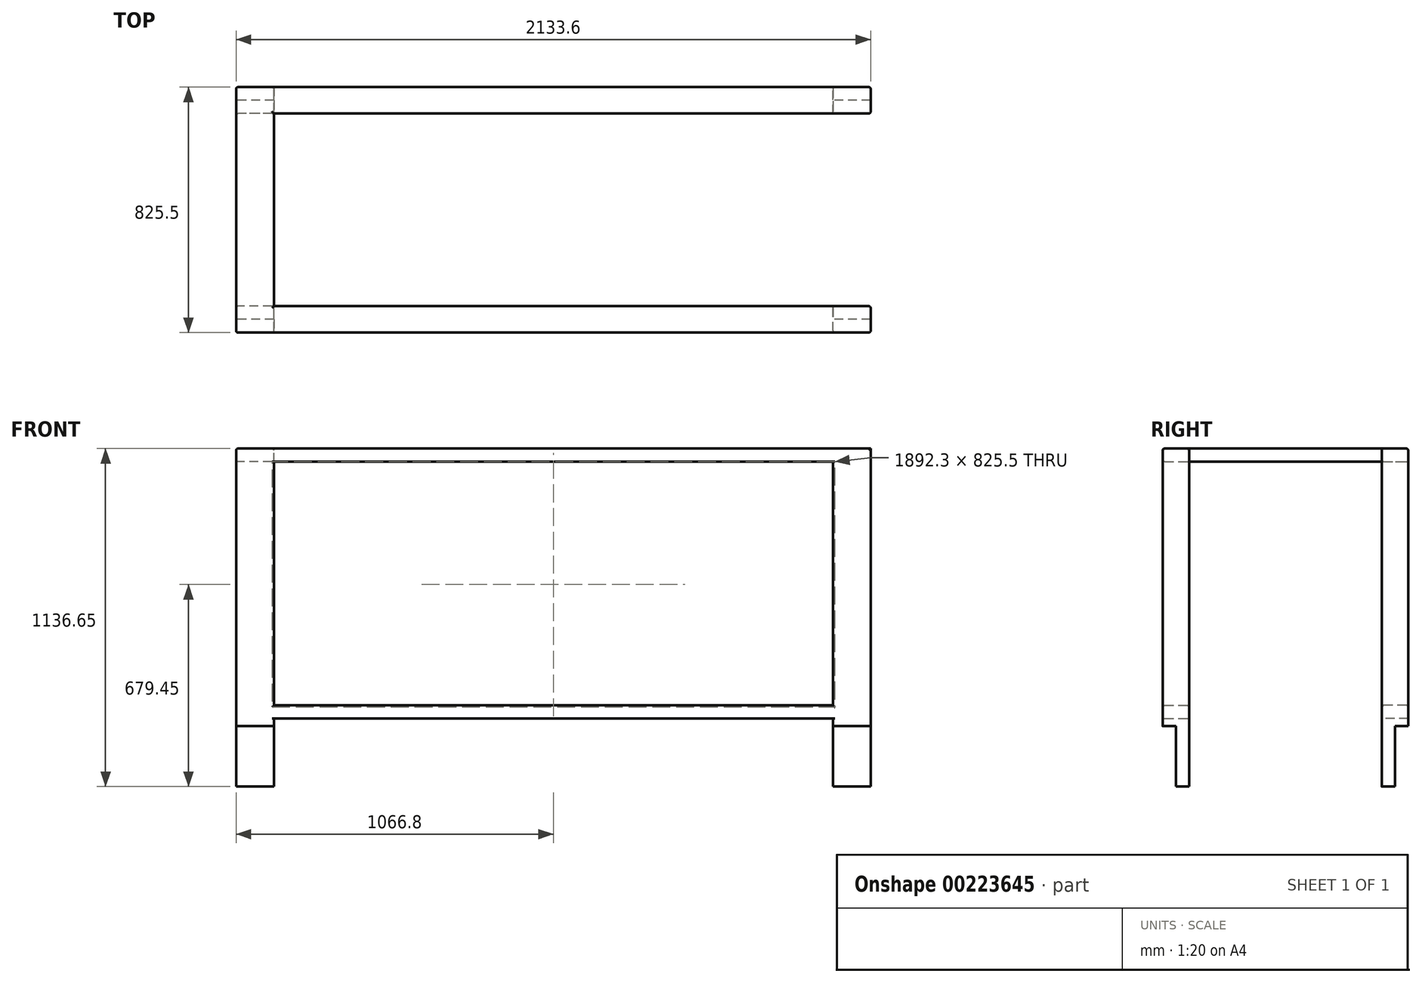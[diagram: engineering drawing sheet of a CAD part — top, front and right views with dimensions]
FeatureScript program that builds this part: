
annotation { "Feature Type Name" : "Feature", "Feature Type Description" : "" }
export const myFeature = defineFeature(function(context is Context, id is Id, definition is map)
    precondition{}
    {
        {
            var Q0;
            Q0=qCreatedBy(makeId("Top.planeOp"),FACE);
            var sketch = newSketch(context, id + "F0", { "sketchPlane" : qUnion([Q0])});
            skLineSegment(sketch, "E0.bottom", {"start": v(75.95, 0) * mm, "end": v(-51.05, 0) * mm});
            skLineSegment(sketch, "E0.top", {"start": v(75.95, -44.45) * mm, "end": v(-51.05, -44.45) * mm});
            skLineSegment(sketch, "E0.left", {"start": v(75.95, 0) * mm, "end": v(75.95, -44.45) * mm});
            skLineSegment(sketch, "E0.right", {"start": v(-51.05, 0) * mm, "end": v(-51.05, -44.45) * mm});
            skSolve(sketch);
        }
        {
            var Q0;
            Q0=makeQuery(id+"F0.imprint","IMPRINT",FACE,{"disambiguationData":[TD([[makeQuery(id+"F0.imprint","IMPRINT",EDGE,{"derivedFrom":sQuery(id+"F0.wireOp",EDGE,"E0.bottom")}),1.0]])]});
            extrude(context, id + "F1", {"entities" : qUnion([Q0]), "depth" : 889 * mm});
        }
        {
            var Q0;
            Q0=makeQuery(id+"F1.opExtrude","CAP_FACE",FACE,{"disambiguationData":[OSD([sQuery(id+"F0.wireOp",EDGE,"E0.bottom"),sQuery(id+"F0.wireOp",EDGE,"E0.top"),sQuery(id+"F0.wireOp",EDGE,"E0.left"),sQuery(id+"F0.wireOp",EDGE,"E0.right")])],"isStart":false});
            var sketch = newSketch(context, id + "F2", { "sketchPlane" : qUnion([Q0])});
            skLineSegment(sketch, "E1.bottom", {"start": v(75.95, 0) * mm, "end": v(-51.05, 0) * mm});
            skLineSegment(sketch, "E1.top", {"start": v(75.95, 44.45) * mm, "end": v(-51.05, 44.45) * mm});
            skLineSegment(sketch, "E1.left", {"start": v(75.95, 0) * mm, "end": v(75.95, 44.45) * mm});
            skLineSegment(sketch, "E1.right", {"start": v(-51.05, 0) * mm, "end": v(-51.05, 44.45) * mm});
            skSolve(sketch);
        }
        {
            var Q0;
            Q0=makeQuery(id+"F2.imprint","IMPRINT",FACE,{"disambiguationData":[TD([[makeQuery(id+"F2.imprint","IMPRINT",EDGE,{"derivedFrom":sQuery(id+"F2.wireOp",EDGE,"E1.bottom")}),-1.0]])]});
            extrude(context, id + "F3", {"entities" : qUnion([Q0]), "oppositeDirection" : true, "depth" : 1092.2 * mm});
        }
        {
            var Q0;
            Q0=makeQuery(id+"F3.boolean.opBoolean","MERGE",FACE,{"derivedFrom":[makeQuery(id+"F1.opExtrude","SWEPT_FACE",FACE,{"disambiguationData":[OSD([sQuery(id+"F0.wireOp",EDGE,"E0.left")])]}),makeQuery(id+"F3.opExtrude","SWEPT_FACE",FACE,{"disambiguationData":[OSD([sQuery(id+"F2.wireOp",EDGE,"E1.left")])]})]});
            var sketch = newSketch(context, id + "F4", { "sketchPlane" : qUnion([Q0])});
            skLineSegment(sketch, "E2.bottom", {"start": v(-44.45, 25.4) * mm, "end": v(44.45, 25.4) * mm});
            skLineSegment(sketch, "E2.top", {"start": v(-44.45, 69.85) * mm, "end": v(44.45, 69.85) * mm});
            skLineSegment(sketch, "E2.left", {"start": v(-44.45, 25.4) * mm, "end": v(-44.45, 69.85) * mm});
            skLineSegment(sketch, "E2.right", {"start": v(44.45, 25.4) * mm, "end": v(44.45, 69.85) * mm});
            skSolve(sketch);
        }
        {
            var Q0;
            Q0=makeQuery(id+"F4.imprint","IMPRINT",FACE,{"disambiguationData":[TD([[makeQuery(id+"F4.imprint","IMPRINT",EDGE,{"derivedFrom":sQuery(id+"F4.wireOp",EDGE,"E2.bottom")}),1.0]])]});
            extrude(context, id + "F5", {"entities" : qUnion([Q0]), "depth" : 1879.6 * mm});
        }
        {
            var Q0;
            Q0=makeQuery(id+"F3.opExtrude","SWEPT_FACE",FACE,{"disambiguationData":[OSD([sQuery(id+"F2.wireOp",EDGE,"E1.right")])]});
            var sketch = newSketch(context, id + "F6", { "sketchPlane" : qUnion([Q0])});
            skLineSegment(sketch, "E3.bottom", {"start": v(-44.45, 889) * mm, "end": v(44.45, 889) * mm});
            skLineSegment(sketch, "E3.top", {"start": v(-44.45, 933.45) * mm, "end": v(44.45, 933.45) * mm});
            skLineSegment(sketch, "E3.left", {"start": v(-44.45, 889) * mm, "end": v(-44.45, 933.45) * mm});
            skLineSegment(sketch, "E3.right", {"start": v(44.45, 889) * mm, "end": v(44.45, 933.45) * mm});
            skSolve(sketch);
        }
        {
            var Q0;
            Q0=makeQuery(id+"F6.imprint","IMPRINT",FACE,{"disambiguationData":[TD([[makeQuery(id+"F6.imprint","IMPRINT",EDGE,{"derivedFrom":sQuery(id+"F6.wireOp",EDGE,"E3.top")}),-1.0]])]});
            extrude(context, id + "F7", {"entities" : qUnion([Q0]), "oppositeDirection" : true, "depth" : 2133.6 * mm});
        }
        {
            var Q0;
            Q0=makeQuery(id+"F7.opExtrude","SWEPT_FACE",FACE,{"disambiguationData":[OSD([sQuery(id+"F6.wireOp",EDGE,"E3.bottom")])]});
            var sketch = newSketch(context, id + "F8", { "sketchPlane" : qUnion([Q0])});
            skLineSegment(sketch, "E4.bottom", {"start": v(2082.55, -44.45) * mm, "end": v(1955.55, -44.45) * mm});
            skLineSegment(sketch, "E4.top", {"start": v(2082.55, 0) * mm, "end": v(1955.55, 0) * mm});
            skLineSegment(sketch, "E4.left", {"start": v(2082.55, -44.45) * mm, "end": v(2082.55, 0) * mm});
            skLineSegment(sketch, "E4.right", {"start": v(1955.55, -44.45) * mm, "end": v(1955.55, 0) * mm});
            skSolve(sketch);
        }
        {
            var Q0;
            Q0=makeQuery(id+"F8.imprint","IMPRINT",FACE,{"disambiguationData":[TD([[makeQuery(id+"F8.imprint","IMPRINT",EDGE,{"derivedFrom":sQuery(id+"F8.wireOp",EDGE,"E4.bottom")}),-1.0]])]});
            extrude(context, id + "F9", {"entities" : qUnion([Q0]), "depth" : 1092.2 * mm});
        }
        {
            var Q0;
            Q0=makeQuery(id+"F7.opExtrude","SWEPT_FACE",FACE,{"disambiguationData":[OSD([sQuery(id+"F6.wireOp",EDGE,"E3.bottom")])]});
            var sketch = newSketch(context, id + "F10", { "sketchPlane" : qUnion([Q0])});
            skLineSegment(sketch, "E5.bottom", {"start": v(2082.55, 44.45) * mm, "end": v(1955.55, 44.45) * mm});
            skLineSegment(sketch, "E5.top", {"start": v(2082.55, 0) * mm, "end": v(1955.55, 0) * mm});
            skLineSegment(sketch, "E5.left", {"start": v(2082.55, 44.45) * mm, "end": v(2082.55, 0) * mm});
            skLineSegment(sketch, "E5.right", {"start": v(1955.55, 44.45) * mm, "end": v(1955.55, 0) * mm});
            skSolve(sketch);
        }
        {
            var Q0;
            Q0=makeQuery(id+"F10.imprint","IMPRINT",FACE,{"disambiguationData":[TD([[makeQuery(id+"F10.imprint","IMPRINT",EDGE,{"derivedFrom":sQuery(id+"F10.wireOp",EDGE,"E5.bottom")}),1.0]])]});
            extrude(context, id + "F11", {"entities" : qUnion([Q0]), "depth" : 889 * mm});
        }
        {
            var Q0;
            Q0=makeQuery(id+"F7.opExtrude","SWEPT_FACE",FACE,{"disambiguationData":[OSD([sQuery(id+"F6.wireOp",EDGE,"E3.top")])]});
            var sketch = newSketch(context, id + "F12", { "sketchPlane" : qUnion([Q0])});
            skLineSegment(sketch, "E6", {"start": v(-51.05, -44.45) * mm, "end": v(-51.05, 44.45) * mm});
            skLineSegment(sketch, "E7", {"start": v(-51.05, 44.45) * mm, "end": v(75.95, 44.45) * mm});
            skLineSegment(sketch, "E8", {"start": v(75.95, 44.45) * mm, "end": v(-51.05, -44.45) * mm});
            skSolve(sketch);
        }
        {
            var Q0;
            Q0=makeQuery(id+"F12.imprint","IMPRINT",FACE,{"disambiguationData":[TD([[makeQuery(id+"F12.imprint","IMPRINT",EDGE,{"derivedFrom":sQuery(id+"F12.wireOp",EDGE,"E6")}),1.0]])]});
            extrude(context, id + "F13", {"entities" : qUnion([Q0]), "oppositeDirection" : true, "depth" : 44.45 * mm});
        }
        {
            var Q0;
            Q0=makeQuery(id+"F13.opExtrude","SWEPT_BODY",BODY,{"disambiguationData":[OSD([sQuery(id+"F12.wireOp",EDGE,"E6"),sQuery(id+"F12.wireOp",EDGE,"E7"),sQuery(id+"F12.wireOp",EDGE,"E8")])]});
            var Q1;
            Q1=makeQuery(id+"F7.opExtrude","SWEPT_BODY",BODY,{"disambiguationData":[OSD([sQuery(id+"F6.wireOp",EDGE,"E3.bottom"),sQuery(id+"F6.wireOp",EDGE,"E3.top"),sQuery(id+"F6.wireOp",EDGE,"E3.left"),sQuery(id+"F6.wireOp",EDGE,"E3.right")])]});
            booleanBodies(context, id + "F14", {"operationType" : BooleanOperationType.SUBTRACTION, "tools" : qUnion([Q0]), "targets" : qUnion([Q1])});
        }
        {
            var Q0;
            Q0=makeQuery(id+"F3.opExtrude","CAP_FACE",FACE,{"disambiguationData":[OSD([sQuery(id+"F2.wireOp",EDGE,"E1.bottom"),sQuery(id+"F2.wireOp",EDGE,"E1.top"),sQuery(id+"F2.wireOp",EDGE,"E1.left"),sQuery(id+"F2.wireOp",EDGE,"E1.right")])],"isStart":true});
            var sketch = newSketch(context, id + "F15", { "sketchPlane" : qUnion([Q0])});
            skLineSegment(sketch, "E9", {"start": v(75.95, 44.45) * mm, "end": v(-51.05, -44.45) * mm});
            skLineSegment(sketch, "E10", {"start": v(-51.05, -44.45) * mm, "end": v(-51.05, 44.45) * mm});
            skLineSegment(sketch, "E11", {"start": v(-51.05, 44.45) * mm, "end": v(75.95, 44.45) * mm});
            skSolve(sketch);
        }
        {
            var Q0;
            {var subQ0=sQuery(id+"F15.wireOp",EDGE,"E10");var subQ1=makeQuery(id+"F3.opExtrude","CAP_EDGE",EDGE,{"disambiguationData":[OSD([sQuery(id+"F2.wireOp",EDGE,"E1.bottom")])],"isStart":true});var subQ2=makeQuery(id+"F15.imprint","INTERSECT",VERTEX,{"derivedFrom":[subQ1,subQ0]});Q0=makeQuery(id+"F15.imprint","IMPRINT",FACE,{"disambiguationData":[TD([[makeQuery(id+"F15.imprint","IMPRINT",EDGE,{"disambiguationData":[TD([[subQ2,1.0]])],"derivedFrom":subQ0}),-1.0]])]});}
            var Q1;
            {var subQ3=sQuery(id+"F15.wireOp",EDGE,"E11");Q1=makeQuery(id+"F15.imprint","IMPRINT",FACE,{"disambiguationData":[TD([[makeQuery(id+"F15.imprint","IMPRINT",EDGE,{"derivedFrom":subQ3}),1.0]])]});}
            extrude(context, id + "F16", {"entities" : qUnion([Q0, Q1]), "depth" : 44.45 * mm});
        }
        {
            var Q0;
            Q0=makeQuery(id+"F16.opExtrude","SWEPT_FACE",FACE,{"disambiguationData":[OSD([sQuery(id+"F15.wireOp",EDGE,"E11")])]});
            extrude(context, id + "F17", {"entities" : qUnion([Q0]), "operationType" : NewBodyOperationType.ADD, "depth" : 323.85 * mm});
        }
        {
            var Q0;
            {var subQ0=sQuery(id+"F15.wireOp",EDGE,"E11");Q0=makeQuery(id+"F17.boolean.opBoolean","MERGE",FACE,{"derivedFrom":[makeQuery(id+"F16.opExtrude","CAP_FACE",FACE,{"disambiguationData":[OSD([sQuery(id+"F15.wireOp",EDGE,"E10"),sQuery(id+"F15.wireOp",EDGE,"E9"),subQ0])],"isStart":false}),makeQuery(id+"F17.opExtrude","SWEPT_FACE",FACE,{"disambiguationData":[OSD([subQ0]),TDD([makeQuery(id+"F16.opExtrude","CAP_EDGE",EDGE,{"disambiguationData":[OSD([subQ0])],"isStart":false})])]})]});}
            var sketch = newSketch(context, id + "F18", { "sketchPlane" : qUnion([Q0])});
            skLineSegment(sketch, "E12", {"start": v(75.95, 368.3) * mm, "end": v(-51.05, 368.3) * mm});
            skLineSegment(sketch, "E13", {"start": v(-51.05, 368.3) * mm, "end": v(-51.05, 457.2) * mm});
            skLineSegment(sketch, "E14", {"start": v(-51.05, 457.2) * mm, "end": v(75.95, 368.3) * mm});
            skSolve(sketch);
        }
        {
            var Q0;
            Q0=makeQuery(id+"F18.imprint","IMPRINT",FACE,{"disambiguationData":[TD([[makeQuery(id+"F18.imprint","IMPRINT",EDGE,{"derivedFrom":sQuery(id+"F18.wireOp",EDGE,"E12")}),-1.0]])]});
            extrude(context, id + "F19", {"entities" : qUnion([Q0]), "operationType" : NewBodyOperationType.ADD, "oppositeDirection" : true, "depth" : 44.45 * mm});
        }
        {
            var Q0;
            Q0=qCreatedBy(makeId("Front.planeOp"),FACE);
            cPlane(context, id + "F20", {"entities" : qUnion([Q0]), "cplaneType" : CPlaneType.OFFSET, "offset" : 368.3 * mm, "oppositeDirection" : true, "width" : 152.4 * mm, "height" : 152.4 * mm});
        }
        {
            var Q0;
            Q0=makeQuery(id+"F7.opExtrude","SWEPT_BODY",BODY,{"disambiguationData":[OSD([sQuery(id+"F6.wireOp",EDGE,"E3.bottom"),sQuery(id+"F6.wireOp",EDGE,"E3.top"),sQuery(id+"F6.wireOp",EDGE,"E3.left"),sQuery(id+"F6.wireOp",EDGE,"E3.right")])]});
            var Q1;
            Q1=makeQuery(id+"F11.opExtrude","SWEPT_BODY",BODY,{"disambiguationData":[OSD([sQuery(id+"F10.wireOp",EDGE,"E5.bottom"),sQuery(id+"F10.wireOp",EDGE,"E5.top"),sQuery(id+"F10.wireOp",EDGE,"E5.left"),sQuery(id+"F10.wireOp",EDGE,"E5.right")])]});
            var Q2;
            Q2=makeQuery(id+"F9.opExtrude","SWEPT_BODY",BODY,{"disambiguationData":[OSD([sQuery(id+"F8.wireOp",EDGE,"E4.bottom"),sQuery(id+"F8.wireOp",EDGE,"E4.top"),sQuery(id+"F8.wireOp",EDGE,"E4.left"),sQuery(id+"F8.wireOp",EDGE,"E4.right")])]});
            var Q3;
            Q3=makeQuery(id+"F5.opExtrude","SWEPT_BODY",BODY,{"disambiguationData":[OSD([sQuery(id+"F4.wireOp",EDGE,"E2.bottom"),sQuery(id+"F4.wireOp",EDGE,"E2.top"),sQuery(id+"F4.wireOp",EDGE,"E2.left"),sQuery(id+"F4.wireOp",EDGE,"E2.right")])]});
            var Q4;
            Q4=makeQuery(id+"F16.opExtrude","SWEPT_BODY",BODY,{"disambiguationData":[OSD([sQuery(id+"F15.wireOp",EDGE,"E10"),sQuery(id+"F15.wireOp",EDGE,"E9"),sQuery(id+"F15.wireOp",EDGE,"E11")])]});
            var Q5;
            Q5=makeQuery(id+"F3.opExtrude","SWEPT_BODY",BODY,{"disambiguationData":[OSD([sQuery(id+"F2.wireOp",EDGE,"E1.bottom"),sQuery(id+"F2.wireOp",EDGE,"E1.top"),sQuery(id+"F2.wireOp",EDGE,"E1.left"),sQuery(id+"F2.wireOp",EDGE,"E1.right")])]});
            var Q6;
            Q6=makeQuery(id+"F1.opExtrude","SWEPT_BODY",BODY,{"disambiguationData":[OSD([sQuery(id+"F0.wireOp",EDGE,"E0.bottom"),sQuery(id+"F0.wireOp",EDGE,"E0.top"),sQuery(id+"F0.wireOp",EDGE,"E0.left"),sQuery(id+"F0.wireOp",EDGE,"E0.right")])]});
            var Q7;
            Q7=qCreatedBy(id+"F20.planeOp",FACE);
            mirror(context, id + "F21", {"operationType" : NewBodyOperationType.ADD, "entities" : qUnion([Q0, Q1, Q2, Q3, Q4, Q5, Q6]), "mirrorPlane" : qUnion([Q7])});
        }
        {
            var Q0;
            Q0=makeQuery(id+"F21.opPattern","COPY",EDGE,{"derivedFrom":makeQuery(id+"F5.opExtrude","SWEPT_EDGE",EDGE,{"disambiguationData":[OSD([sQuery(id+"F0.wireOp",EDGE,"E0.top"),sQuery(id+"F0.wireOp",EDGE,"E0.left"),sQuery(id+"F4.wireOp",EDGE,"E2.top"),sQuery(id+"F4.wireOp",EDGE,"E2.left")])]}),"instanceName":"1"});
            var Q1;
            Q1=makeQuery(id+"F21.opPattern","COPY",EDGE,{"derivedFrom":makeQuery(id+"F5.opExtrude","SWEPT_EDGE",EDGE,{"disambiguationData":[OSD([sQuery(id+"F2.wireOp",EDGE,"E1.top"),sQuery(id+"F2.wireOp",EDGE,"E1.left"),sQuery(id+"F4.wireOp",EDGE,"E2.top"),sQuery(id+"F4.wireOp",EDGE,"E2.right")])]}),"instanceName":"1"});
            var Q2;
            Q2=makeQuery(id+"F21.opPattern","COPY",EDGE,{"derivedFrom":makeQuery(id+"F7.opExtrude","SWEPT_EDGE",EDGE,{"disambiguationData":[OSD([sQuery(id+"F6.wireOp",EDGE,"E3.top"),sQuery(id+"F6.wireOp",EDGE,"E3.right")])]}),"instanceName":"1"});
            var Q3;
            Q3=makeQuery(id+"F21.opPattern","COPY",EDGE,{"derivedFrom":makeQuery(id+"F7.opExtrude","SWEPT_EDGE",EDGE,{"disambiguationData":[OSD([sQuery(id+"F6.wireOp",EDGE,"E3.top"),sQuery(id+"F6.wireOp",EDGE,"E3.left")])]}),"instanceName":"1"});
            var Q4;
            Q4=makeQuery(id+"F21.opPattern","COPY",EDGE,{"derivedFrom":makeQuery(id+"F7.opExtrude","CAP_EDGE",EDGE,{"disambiguationData":[OSD([sQuery(id+"F6.wireOp",EDGE,"E3.top")])],"isStart":false}),"instanceName":"1"});
            var Q5;
            Q5=makeQuery(id+"F21.boolean.opBoolean","MERGE",EDGE,{"derivedFrom":[makeQuery(id+"F21.opPattern","COPY",EDGE,{"derivedFrom":makeQuery(id+"F7.opExtrude","CAP_EDGE",EDGE,{"disambiguationData":[OSD([sQuery(id+"F6.wireOp",EDGE,"E3.right")])],"isStart":false}),"instanceName":"1"}),makeQuery(id+"F21.opPattern","COPY",EDGE,{"derivedFrom":makeQuery(id+"F11.opExtrude","SWEPT_EDGE",EDGE,{"disambiguationData":[OSD([sQuery(id+"F10.wireOp",EDGE,"E5.bottom"),sQuery(id+"F10.wireOp",EDGE,"E5.left")])]}),"instanceName":"1"})]});
            var Q6;
            Q6=makeQuery(id+"F21.boolean.opBoolean","MERGE",EDGE,{"derivedFrom":[makeQuery(id+"F21.opPattern","COPY",EDGE,{"derivedFrom":makeQuery(id+"F7.opExtrude","CAP_EDGE",EDGE,{"disambiguationData":[OSD([sQuery(id+"F6.wireOp",EDGE,"E3.left")])],"isStart":false}),"instanceName":"1"}),makeQuery(id+"F21.opPattern","COPY",EDGE,{"derivedFrom":makeQuery(id+"F9.opExtrude","SWEPT_EDGE",EDGE,{"disambiguationData":[OSD([sQuery(id+"F8.wireOp",EDGE,"E4.bottom"),sQuery(id+"F8.wireOp",EDGE,"E4.left")])]}),"instanceName":"1"})]});
            var Q7;
            {var subQ0=sQuery(id+"F6.wireOp",EDGE,"E3.right");var subQ1=sQuery(id+"F10.wireOp",EDGE,"E5.bottom");var subQ2=sQuery(id+"F10.wireOp",EDGE,"E5.right");var subQ3=sQuery(id+"F6.wireOp",EDGE,"E3.bottom");Q7=makeQuery(id+"F21.boolean.opBoolean","SPLIT",EDGE,{"disambiguationData":[TD([makeQuery(id+"F21.opPattern","COPY",FACE,{"derivedFrom":makeQuery(id+"F5.opExtrude","SWEPT_FACE",FACE,{"disambiguationData":[OSD([sQuery(id+"F4.wireOp",EDGE,"E2.top")])]}),"instanceName":"1"})])],"derivedFrom":makeQuery(id+"F21.opPattern","COPY",EDGE,{"derivedFrom":makeQuery(id+"F11.opExtrude","SWEPT_EDGE",EDGE,{"disambiguationData":[OSD([subQ3,subQ0,subQ1,subQ2])]}),"instanceName":"1"})});}
            var Q8;
            Q8=makeQuery(id+"F9.opExtrude","SWEPT_EDGE",EDGE,{"disambiguationData":[OSD([sQuery(id+"F2.wireOp",EDGE,"E1.top"),sQuery(id+"F2.wireOp",EDGE,"E1.right"),sQuery(id+"F6.wireOp",EDGE,"E3.bottom"),sQuery(id+"F6.wireOp",EDGE,"E3.left"),sQuery(id+"F8.wireOp",EDGE,"E4.bottom"),sQuery(id+"F8.wireOp",EDGE,"E4.right")])]});
            var Q9;
            Q9=makeQuery(id+"F9.opExtrude","SWEPT_EDGE",EDGE,{"disambiguationData":[OSD([sQuery(id+"F8.wireOp",EDGE,"E4.bottom"),sQuery(id+"F8.wireOp",EDGE,"E4.left")])]});
            var Q10;
            Q10=makeQuery(id+"F11.opExtrude","SWEPT_EDGE",EDGE,{"disambiguationData":[OSD([sQuery(id+"F10.wireOp",EDGE,"E5.bottom"),sQuery(id+"F10.wireOp",EDGE,"E5.left")])]});
            var Q11;
            Q11=makeQuery(id+"F7.opExtrude","SWEPT_EDGE",EDGE,{"disambiguationData":[OSD([sQuery(id+"F6.wireOp",EDGE,"E3.top"),sQuery(id+"F6.wireOp",EDGE,"E3.right")])]});
            var Q12;
            Q12=makeQuery(id+"F7.opExtrude","SWEPT_EDGE",EDGE,{"disambiguationData":[OSD([sQuery(id+"F6.wireOp",EDGE,"E3.top"),sQuery(id+"F6.wireOp",EDGE,"E3.left")])]});
            var Q13;
            {var subQ0=sQuery(id+"F15.wireOp",EDGE,"E11");var subQ1=sQuery(id+"F15.wireOp",EDGE,"E9");var subQ2=sQuery(id+"F2.wireOp",EDGE,"E1.left");var subQ3=makeQuery(id+"F17.opExtrude","SWEPT_EDGE",EDGE,{"disambiguationData":[OSD([subQ2,subQ1,subQ0]),TDD([makeQuery(id+"F16.opExtrude","CAP_VERTEX",VERTEX,{"disambiguationData":[OSD([subQ2,subQ1,subQ0])],"isStart":false})])]});Q13=makeQuery(id+"F21.boolean.opBoolean","MERGE",EDGE,{"derivedFrom":[subQ3,makeQuery(id+"F21.opPattern","COPY",EDGE,{"derivedFrom":subQ3,"instanceName":"1"})]});}
            var Q14;
            {var subQ0=sQuery(id+"F15.wireOp",EDGE,"E11");var subQ1=sQuery(id+"F15.wireOp",EDGE,"E10");var subQ2=makeQuery(id+"F19.boolean.opBoolean","MERGE",EDGE,{"derivedFrom":[makeQuery(id+"F17.boolean.opBoolean","MERGE",EDGE,{"derivedFrom":[makeQuery(id+"F16.opExtrude","CAP_EDGE",EDGE,{"disambiguationData":[OSD([subQ1])],"isStart":false}),makeQuery(id+"F17.opExtrude","SWEPT_EDGE",EDGE,{"disambiguationData":[OSD([subQ1,subQ0]),TDD([makeQuery(id+"F16.opExtrude","CAP_VERTEX",VERTEX,{"disambiguationData":[OSD([subQ1,subQ0])],"isStart":false})])]})]}),makeQuery(id+"F19.opExtrude","CAP_EDGE",EDGE,{"disambiguationData":[OSD([sQuery(id+"F18.wireOp",EDGE,"E13")])],"isStart":true})]});Q14=makeQuery(id+"F21.boolean.opBoolean","MERGE",EDGE,{"derivedFrom":[subQ2,makeQuery(id+"F21.opPattern","COPY",EDGE,{"derivedFrom":subQ2,"instanceName":"1"})]});}
            var Q15;
            {var subQ0=sQuery(id+"F0.wireOp",EDGE,"E0.left");var subQ1=sQuery(id+"F0.wireOp",EDGE,"E0.top");Q15=makeQuery(id+"F21.boolean.opBoolean","SPLIT",EDGE,{"disambiguationData":[TD([makeQuery(id+"F21.opPattern","COPY",FACE,{"derivedFrom":makeQuery(id+"F5.opExtrude","SWEPT_FACE",FACE,{"disambiguationData":[OSD([sQuery(id+"F4.wireOp",EDGE,"E2.top")])]}),"instanceName":"1"})])],"derivedFrom":makeQuery(id+"F21.opPattern","COPY",EDGE,{"derivedFrom":makeQuery(id+"F1.opExtrude","SWEPT_EDGE",EDGE,{"disambiguationData":[OSD([subQ1,subQ0])]}),"instanceName":"1"})});}
            var Q16;
            {var subQ0=sQuery(id+"F6.wireOp",EDGE,"E3.right");Q16=makeQuery(id+"F21.boolean.opBoolean","MERGE",EDGE,{"derivedFrom":[makeQuery(id+"F21.opPattern","COPY",EDGE,{"derivedFrom":makeQuery(id+"F1.opExtrude","SWEPT_EDGE",EDGE,{"disambiguationData":[OSD([sQuery(id+"F0.wireOp",EDGE,"E0.top"),sQuery(id+"F0.wireOp",EDGE,"E0.right")])]}),"instanceName":"1"}),makeQuery(id+"F21.opPattern","COPY",EDGE,{"derivedFrom":makeQuery(id+"F14.opBoolean","MERGE",EDGE,{"derivedFrom":[makeQuery(id+"F7.opExtrude","CAP_EDGE",EDGE,{"disambiguationData":[OSD([subQ0])],"isStart":true}),makeQuery(id+"F13.opExtrude","SWEPT_EDGE",EDGE,{"disambiguationData":[OSD([sQuery(id+"F6.wireOp",EDGE,"E3.top"),subQ0,sQuery(id+"F12.wireOp",EDGE,"E6"),sQuery(id+"F12.wireOp",EDGE,"E8")])]})]}),"instanceName":"1"}),makeQuery(id+"F21.opPattern","COPY",EDGE,{"derivedFrom":makeQuery(id+"F16.opExtrude","SWEPT_EDGE",EDGE,{"disambiguationData":[OSD([sQuery(id+"F15.wireOp",EDGE,"E10"),sQuery(id+"F15.wireOp",EDGE,"E9")])]}),"instanceName":"1"})]});}
            var Q17;
            {var subQ0=sQuery(id+"F2.wireOp",EDGE,"E1.left");var subQ1=sQuery(id+"F2.wireOp",EDGE,"E1.top");Q17=makeQuery(id+"F21.boolean.opBoolean","SPLIT",EDGE,{"disambiguationData":[TD([makeQuery(id+"F21.opPattern","COPY",FACE,{"derivedFrom":makeQuery(id+"F5.opExtrude","SWEPT_FACE",FACE,{"disambiguationData":[OSD([sQuery(id+"F4.wireOp",EDGE,"E2.top")])]}),"instanceName":"1"})])],"derivedFrom":makeQuery(id+"F21.opPattern","COPY",EDGE,{"derivedFrom":makeQuery(id+"F3.opExtrude","SWEPT_EDGE",EDGE,{"disambiguationData":[OSD([subQ1,subQ0])]}),"instanceName":"1"})});}
            var Q18;
            Q18=makeQuery(id+"F5.opExtrude","SWEPT_EDGE",EDGE,{"disambiguationData":[OSD([sQuery(id+"F2.wireOp",EDGE,"E1.top"),sQuery(id+"F2.wireOp",EDGE,"E1.left"),sQuery(id+"F4.wireOp",EDGE,"E2.top"),sQuery(id+"F4.wireOp",EDGE,"E2.right")])]});
            var Q19;
            Q19=makeQuery(id+"F5.opExtrude","SWEPT_EDGE",EDGE,{"disambiguationData":[OSD([sQuery(id+"F0.wireOp",EDGE,"E0.top"),sQuery(id+"F0.wireOp",EDGE,"E0.left"),sQuery(id+"F4.wireOp",EDGE,"E2.top"),sQuery(id+"F4.wireOp",EDGE,"E2.left")])]});
            var Q20;
            Q20=makeQuery(id+"F3.opExtrude","SWEPT_EDGE",EDGE,{"disambiguationData":[OSD([sQuery(id+"F2.wireOp",EDGE,"E1.top"),sQuery(id+"F2.wireOp",EDGE,"E1.left")])]});
            var Q21;
            Q21=makeQuery(id+"F3.opExtrude","SWEPT_EDGE",EDGE,{"disambiguationData":[OSD([sQuery(id+"F2.wireOp",EDGE,"E1.top"),sQuery(id+"F2.wireOp",EDGE,"E1.right")])]});
            var Q22;
            Q22=makeQuery(id+"F1.opExtrude","SWEPT_EDGE",EDGE,{"disambiguationData":[OSD([sQuery(id+"F0.wireOp",EDGE,"E0.top"),sQuery(id+"F0.wireOp",EDGE,"E0.left")])]});
            var Q23;
            Q23=makeQuery(id+"F1.opExtrude","SWEPT_EDGE",EDGE,{"disambiguationData":[OSD([sQuery(id+"F0.wireOp",EDGE,"E0.top"),sQuery(id+"F0.wireOp",EDGE,"E0.right")])]});
            var Q24;
            Q24=makeQuery(id+"F16.opExtrude","SWEPT_EDGE",EDGE,{"disambiguationData":[OSD([sQuery(id+"F15.wireOp",EDGE,"E10"),sQuery(id+"F15.wireOp",EDGE,"E9")])]});
            var Q25;
            Q25=makeQuery(id+"F21.opPattern","COPY",EDGE,{"derivedFrom":makeQuery(id+"F3.opExtrude","SWEPT_EDGE",EDGE,{"disambiguationData":[OSD([sQuery(id+"F2.wireOp",EDGE,"E1.top"),sQuery(id+"F2.wireOp",EDGE,"E1.right")])]}),"instanceName":"1"});
            var Q26;
            Q26=makeQuery(id+"F11.opExtrude","SWEPT_EDGE",EDGE,{"disambiguationData":[OSD([sQuery(id+"F6.wireOp",EDGE,"E3.bottom"),sQuery(id+"F6.wireOp",EDGE,"E3.right"),sQuery(id+"F10.wireOp",EDGE,"E5.bottom"),sQuery(id+"F10.wireOp",EDGE,"E5.right")])]});
            fillet(context, id + "F22", {"entities" : qUnion([Q0, Q1, Q2, Q3, Q4, Q5, Q6, Q7, Q8, Q9, Q10, Q11, Q12, Q13, Q14, Q15, Q16, Q17, Q18, Q19, Q20, Q21, Q22, Q23, Q24, Q25, Q26]), "radius" : 6.35 * mm, "tangentPropagation" : true, "allowEdgeOverflow" : false});
        }
    });
